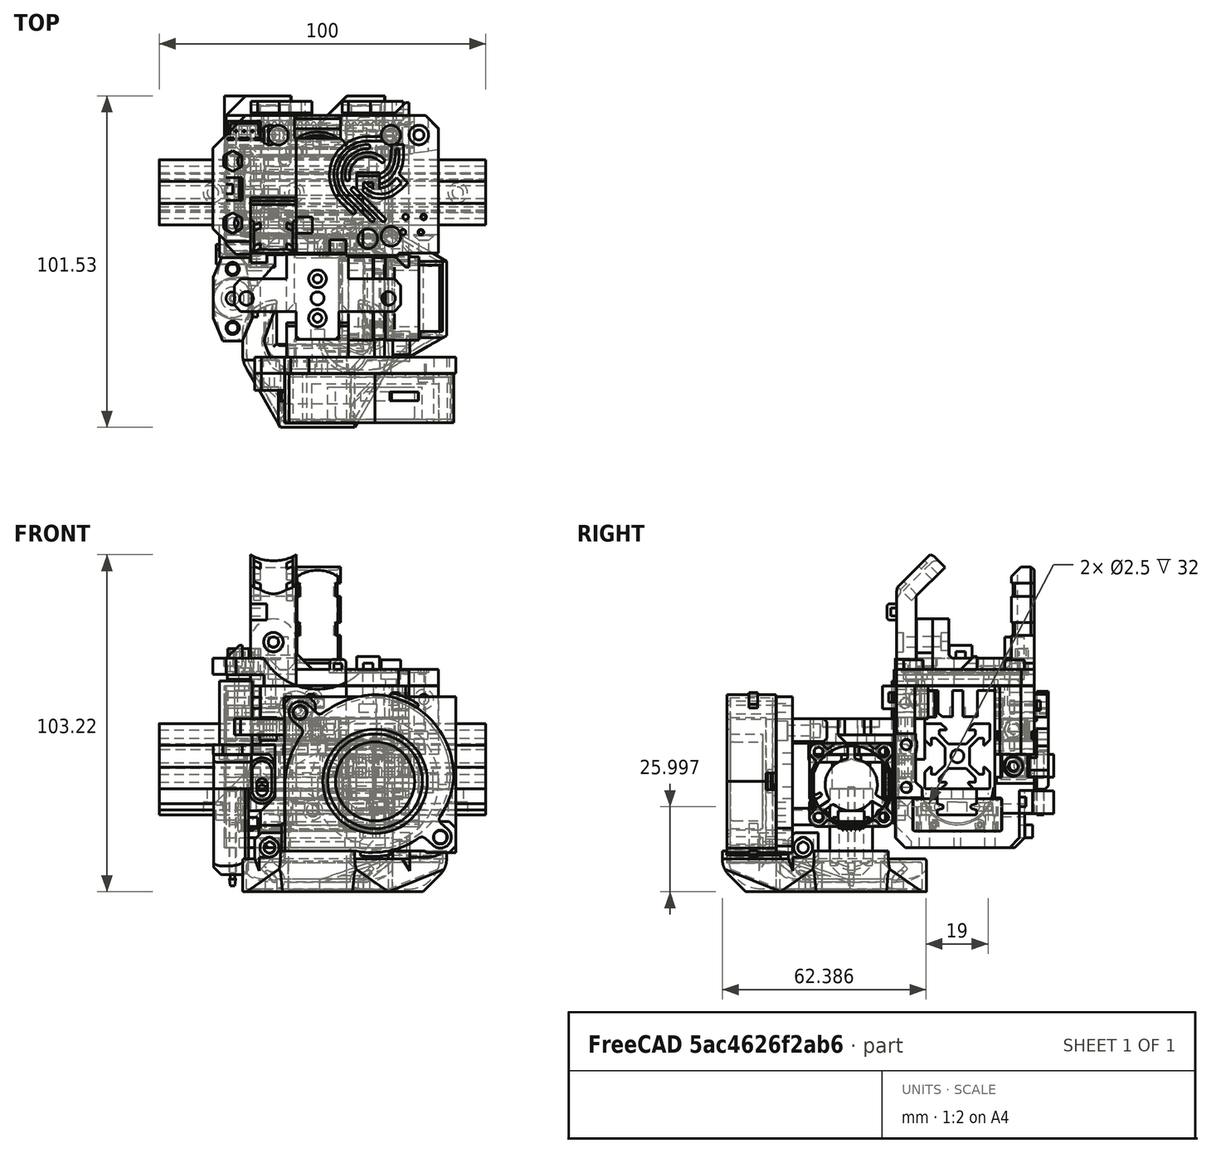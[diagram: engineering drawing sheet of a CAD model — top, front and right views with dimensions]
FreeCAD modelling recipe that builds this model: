
FCSTD DOCUMENT  (FreeCAD 0.18R16146 (Git))
Label: mosquito-mount
License: All rights reserved
LicenseURL: http://en.wikipedia.org/wiki/All_rights_reserved
objects: Part::Box×89, Part::Cylinder×71, Part::Cut×71, Part::MultiFuse×55, Part::Chamfer×54, Part::Feature×39, Mesh::Feature×1
note: 379 computed .brp shape members not serialized (recipe doc carries the construction recipe); baked Part::Feature solids carry a one-line shape summary decoded from their .brp

FEATURE [Part::Box] Box  label="Cube"
  AttacherType = Attacher::AttachEngine3D
  Height = 10
  Length = 45.4
  Width = 27
FEATURE [Part::Cylinder] Cylinder
  Angle = 360
  AttacherType = Attacher::AttachEngine3D
  Height = 10
  Placement = pos=(12.7,3.5,0) rot=(0,0,1;0rad)
  Radius = 2
FEATURE [Part::Cylinder] Cylinder001
  Angle = 360
  AttacherType = Attacher::AttachEngine3D
  Height = 10
  Placement = pos=(32.7,3.5,0) rot=(0,0,1;0rad)
  Radius = 2
FEATURE [Part::Cylinder] Cylinder002
  Angle = 360
  AttacherType = Attacher::AttachEngine3D
  Height = 10
  Placement = pos=(32.7,23.5,0) rot=(0,0,1;0rad)
  Radius = 2
FEATURE [Part::Cylinder] Cylinder003
  Angle = 360
  AttacherType = Attacher::AttachEngine3D
  Height = 10
  Placement = pos=(12.7,23.5,0) rot=(0,0,1;0rad)
  Radius = 2
FEATURE [Part::MultiFuse] Fusion
  Shapes = -> [Cylinder003,Cylinder002,Cylinder001,Cylinder]
FEATURE [Part::Cut] Cut  label="12H-block-ref"
  Base = -> Box
  Placement = pos=(-22.7,-13.5,5) rot=(0,0,1;0rad)
  Tool = -> Fusion
FEATURE [Part::Feature] Part__Feature072001  label="hemera-mount"
  shape: bbox 65.55 x 51.14 x 89.74 mm, 349 faces (baked)
FEATURE [Part::Feature] Part__Feature  label="mosquito"
  Placement = pos=(-7e-15,-32.5,3.5) rot=(1,0,0;1.5708rad)
  shape: bbox 18.85 x 27 x 47 mm, 429 faces, 0 solids (baked)
FEATURE [Part::Box] Box001  label="Cube001"
  AttacherType = Attacher::AttachEngine3D
  Height = 49.5
  Length = 56
  Placement = pos=(-28,-19,0) rot=(0,0,1;0rad)
  Width = 38
FEATURE [Part::Box] Box004  label="block-slot"
  AttacherType = Attacher::AttachEngine3D
  Height = 10.2
  Length = 60
  Placement = pos=(-22.8,-13.6,5) rot=(0,0,1;0rad)
  Width = 27.2
FEATURE [Part::Cylinder] Cylinder004
  Angle = 360
  AttacherType = Attacher::AttachEngine3D
  Height = 26
  Placement = pos=(-12,0,18) rot=(0,-1,0;1.5708rad)
  Radius = 11
FEATURE [Part::Box] Box005  label="Cube002"
  AttacherType = Attacher::AttachEngine3D
  Height = 39
  Length = 72
  Placement = pos=(-32,-13.05,18) rot=(0,0,1;0rad)
  Width = 24.5
FEATURE [Part::Chamfer] Chamfer
  Base = -> Box005
  Edges = 1 edges r=2: [Edge9]
  Placement = pos=(0,0,0.1) rot=(0,0,1;0rad)
FEATURE [Part::Chamfer] Chamfer001
  Base = -> Box004
  Edges = 4 edges r=0.4: [Edge9,Edge10,Edge11,Edge12]
FEATURE [Part::Box] Box006  label="Cube003"
  AttacherType = Attacher::AttachEngine3D
  Height = 10
  Length = 56
  Placement = pos=(-22.8,-11,10) rot=(0,0,1;0rad)
  Width = 22
FEATURE [Mesh::Feature] sherpa_mini_assy_a1
  Placement = pos=(-4.35,-22.5,53) rot=(1,0,0;1.5708rad)
FEATURE [Part::Cut] Cut001
  Base = -> Box001
  Tool = -> Chamfer001
FEATURE [Part::Cut] Cut002
  Base = -> Cut001
  Tool = -> Box006
FEATURE [Part::Cut] Cut003
  Base = -> Cut002
  Tool = -> Cylinder004
FEATURE [Part::Cut] Cut004
  Base = -> Cut003
  Tool = -> Chamfer
FEATURE [Part::Box] Box007  label="Cube004"
  AttacherType = Attacher::AttachEngine3D
  Height = 32.15
  Length = 56
  Placement = pos=(-28,19,17.35) rot=(0,0,1;0rad)
  Width = 4.53
FEATURE [Part::Box] Box008  label="Cube005"
  AttacherType = Attacher::AttachEngine3D
  Height = 6.97
  Length = 22
  Placement = pos=(-1.5,18.5,10.38) rot=(0,0,1;0rad)
  Width = 11
FEATURE [Part::Box] Box009  label="Cube006"
  AttacherType = Attacher::AttachEngine3D
  Height = 6.97
  Length = 20
  Placement = pos=(-28,23.5,21.6) rot=(0,0,1;0rad)
  Width = 6
FEATURE [Part::Box] Box010  label="Cube007"
  AttacherType = Attacher::AttachEngine3D
  Height = 6.97
  Length = 6
  Placement = pos=(10.5,23.5,10.38) rot=(0,0,1;0rad)
  Width = 3
FEATURE [Part::Box] Box011  label="Cube008"
  AttacherType = Attacher::AttachEngine3D
  Height = 6.97
  Length = 6
  Placement = pos=(-17.5,23.5,21.6) rot=(0,0,1;0rad)
  Width = 3
FEATURE [Part::Cut] Cut005
  Base = -> Box009
  Tool = -> Box011
FEATURE [Part::Cut] Cut006
  Base = -> Box008
  Tool = -> Box010
FEATURE [Part::Chamfer] Chamfer002
  Base = -> Cut006
  Edges = 1 edges r=10.5: [Edge3]
FEATURE [Part::Chamfer] Chamfer003
  Base = -> Cut005
  Edges = 1 edges r=5.97: [Edge3]
FEATURE [Part::Box] Box012  label="Cube009"
  AttacherType = Attacher::AttachEngine3D
  Height = 10
  Length = 12
  Placement = pos=(-24,-1,0) rot=(0,0,1;0rad)
  Width = 2
FEATURE [Part::Cut] Cut007
  Base = -> Cut004
  Tool = -> Box012
FEATURE [Part::MultiFuse] Fusion001
  Shapes = -> [Cut007,Box007]
FEATURE [Part::Box] Box013  label="Cube010"
  AttacherType = Attacher::AttachEngine3D
  Height = 6.97
  Length = 29
  Placement = pos=(-28,3.61,32.63) rot=(0,0,1;0rad)
  Width = 10
FEATURE [Part::Box] Box014  label="Cube011"
  AttacherType = Attacher::AttachEngine3D
  Height = 6.97
  Length = 23
  Placement = pos=(5,3.61,21.6) rot=(0,0,1;0rad)
  Width = 10
FEATURE [Part::Box] Box015  label="Cube012"
  AttacherType = Attacher::AttachEngine3D
  Height = 6.97
  Length = 17
  Placement = pos=(-8,9,21.6) rot=(0,0,1;0rad)
  Width = 22
FEATURE [Part::Box] Box016  label="Cube013"
  AttacherType = Attacher::AttachEngine3D
  Height = 6.97
  Length = 17
  Placement = pos=(1,7.5,32.63) rot=(0,0,1;0rad)
  Width = 20
FEATURE [Part::Cut] Cut008
  Base = -> Fusion001
  Tool = -> Box016
FEATURE [Part::Cut] Cut009
  Base = -> Cut008
  Tool = -> Box015
FEATURE [Part::Box] Box017  label="Cube014"
  AttacherType = Attacher::AttachEngine3D
  Height = 6.97
  Length = 23
  Placement = pos=(5,20.61,21.6) rot=(0,0,1;0rad)
  Width = 10
FEATURE [Part::Box] Box018  label="Cube015"
  AttacherType = Attacher::AttachEngine3D
  Height = 5.97
  Length = 29
  Placement = pos=(-28,20.61,33.63) rot=(0,0,1;0rad)
  Width = 10
FEATURE [Part::Cut] Cut010
  Base = -> Cut009
  Tool = -> Box013
FEATURE [Part::Cut] Cut011
  Base = -> Cut010
  Tool = -> Box014
FEATURE [Part::Feature] Part__Feature072001001  label="hemera-mount001"
  shape: bbox 65.55 x 51.14 x 89.74 mm, 349 faces (baked)
FEATURE [Part::Feature] Part__Feature072001002  label="hemera-mount002"
  shape: bbox 65.55 x 51.14 x 89.74 mm, 349 faces (baked)
FEATURE [Part::Cut] Cut012
  Base = -> Box017
  Tool = -> Part__Feature072001002
FEATURE [Part::Cut] Cut013
  Base = -> Box018
  Tool = -> Part__Feature072001001
FEATURE [Part::Feature] Cut013001  label="Cut014"
  Placement = pos=(0,0,-1) rot=(0,0,1;0rad)
  shape: bbox 29 x 10 x 5.971 mm, 63 faces (baked)
FEATURE [Part::Cut] Cut013002
  Base = -> Cut011
  Tool = -> Cut012
FEATURE [Part::MultiFuse] Fusion002
  Shapes = -> [Cut013001,Cut013]
FEATURE [Part::Cut] Cut013003
  Base = -> Cut013002
  Tool = -> Fusion002
FEATURE [Part::Cylinder] Cylinder005
  Angle = 360
  AttacherType = Attacher::AttachEngine3D
  Height = 6
  Placement = pos=(-5,17.57,36.115) rot=(0,1,0;1.5708rad)
  Radius = 2.1
FEATURE [Part::Cylinder] Cylinder006
  Angle = 360
  AttacherType = Attacher::AttachEngine3D
  Height = 6
  Placement = pos=(9,17.57,25.08) rot=(0,1,0;1.5708rad)
  Radius = 2.1
FEATURE [Part::Cylinder] Cylinder007
  Angle = 360
  AttacherType = Attacher::AttachEngine3D
  Height = 32
  Placement = pos=(-6e-15,17.57,25.08) rot=(0,1,0;1.5708rad)
  Radius = 1.65
FEATURE [Part::Cylinder] Cylinder008
  Angle = 360
  AttacherType = Attacher::AttachEngine3D
  Height = 37
  Placement = pos=(-29,17.57,36.115) rot=(0,1,0;1.5708rad)
  Radius = 1.65
FEATURE [Part::Cut] Cut013004
  Base = -> Cut013003
  Tool = -> Cylinder008
FEATURE [Part::Cut] Cut013005
  Base = -> Cut013004
  Tool = -> Cylinder007
FEATURE [Part::Cylinder] Cylinder009
  Angle = 360
  AttacherType = Attacher::AttachEngine3D
  Height = 3
  Placement = pos=(25,17.57,25.08) rot=(0,1,0;1.5708rad)
  Radius = 3
FEATURE [Part::Cylinder] Cylinder010
  Angle = 360
  AttacherType = Attacher::AttachEngine3D
  Height = 3
  Placement = pos=(-28,17.57,36.115) rot=(0,1,0;1.5708rad)
  Radius = 3
FEATURE [Part::MultiFuse] Fusion003
  Shapes = -> [Cylinder010,Cylinder009]
FEATURE [Part::Cut] Cut013006
  Base = -> Cut013005
  Tool = -> Fusion003
FEATURE [Part::MultiFuse] Fusion004
  Shapes = -> [Cylinder006,Cylinder005]
FEATURE [Part::Cut] Cut013007
  Base = -> Cut013006
  Tool = -> Fusion004
FEATURE [Part::Box] Box019  label="Cube016"
  AttacherType = Attacher::AttachEngine3D
  Height = 19.65
  Length = 10.5
  Placement = pos=(17.5,-20.5,15.2) rot=(0,0,1;0rad)
  Width = 10
FEATURE [Part::Box] Box020  label="Cube017"
  AttacherType = Attacher::AttachEngine3D
  Height = 28
  Length = 10.5
  Placement = pos=(-28,-20,26) rot=(0,0,1;0rad)
  Width = 10
FEATURE [Part::Cylinder] Cylinder011
  Angle = 360
  AttacherType = Attacher::AttachEngine3D
  Height = 14.5
  Placement = pos=(3,-15.83,18.41) rot=(0,1,0;1.5708rad)
  Radius = 1.65
FEATURE [Part::Cylinder] Cylinder012
  Angle = 360
  AttacherType = Attacher::AttachEngine3D
  Height = 14.5
  Placement = pos=(3,-15.83,31.54) rot=(0,1,0;1.5708rad)
  Radius = 1.65
FEATURE [Part::Feature] Part__Feature044  label="duct-pos-pref"
  Placement = pos=(0.025,-32.5,-13.5) rot=(0,0,1;1.5708rad)
  shape: bbox 38.99 x 46.01 x 18.01 mm, 128 faces (baked)
FEATURE [Part::Cylinder] Cylinder013
  Angle = 360
  AttacherType = Attacher::AttachEngine3D
  Height = 14.5
  Placement = pos=(-3,-15.82,29.97) rot=(0,-1,0;1.5708rad)
  Radius = 1.65
FEATURE [Part::Cylinder] Cylinder014
  Angle = 360
  AttacherType = Attacher::AttachEngine3D
  Height = 19.5
  Placement = pos=(2,-15.82,44.28) rot=(0,-1,0;1.5708rad)
  Radius = 1.65
FEATURE [Part::Cylinder] Cylinder015
  Angle = 360
  AttacherType = Attacher::AttachEngine3D
  Height = 19.5
  Placement = pos=(2,-15.82,44.28) rot=(0,-1,0;1.5708rad)
  Radius = 3
FEATURE [Part::Cylinder] Cylinder016
  Angle = 360
  AttacherType = Attacher::AttachEngine3D
  Height = 14.5
  Placement = pos=(-3,-15.82,29.97) rot=(0,-1,0;1.5708rad)
  Radius = 3
FEATURE [Part::Cylinder] Cylinder017
  Angle = 360
  AttacherType = Attacher::AttachEngine3D
  Height = 14.5
  Placement = pos=(3,-15.83,31.54) rot=(0,1,0;1.5708rad)
  Radius = 3
FEATURE [Part::Cylinder] Cylinder018
  Angle = 360
  AttacherType = Attacher::AttachEngine3D
  Height = 14.5
  Placement = pos=(3,-15.83,18.41) rot=(0,1,0;1.5708rad)
  Radius = 3
FEATURE [Part::Box] Box021  label="Cube018"
  AttacherType = Attacher::AttachEngine3D
  Height = 5.5
  Length = 2
  Placement = pos=(10,-23.5,28.79) rot=(0,0,1;0rad)
  Width = 20
FEATURE [Part::Box] Box022  label="Cube019"
  AttacherType = Attacher::AttachEngine3D
  Height = 5.5
  Length = 2
  Placement = pos=(-3,-23.5,41.53) rot=(0,0,1;0rad)
  Width = 20
FEATURE [Part::Box] Box023  label="Cube020"
  AttacherType = Attacher::AttachEngine3D
  Height = 5.5
  Length = 2
  Placement = pos=(-10,-23.5,27.22) rot=(0,0,1;0rad)
  Width = 20
FEATURE [Part::Box] Box024  label="Cube021"
  AttacherType = Attacher::AttachEngine3D
  Height = 5.5
  Length = 2
  Placement = pos=(8,-23.5,15.66) rot=(0,0,1;0rad)
  Width = 20
FEATURE [Part::Box] Box025  label="Cube022"
  AttacherType = Attacher::AttachEngine3D
  Height = 10
  Length = 10
  Placement = pos=(18,-13.5,39.5) rot=(0,0,1;0rad)
  Width = 4.5
FEATURE [Part::Chamfer] Chamfer004  label="top-atd"
  Base = -> Box025
  Edges = 1 edges r=4.05: [Edge3]
FEATURE [Part::Feature] Fusion015  label="bltouch-pref"
  Placement = pos=(-26,-32.5,28.45) rot=(0,0,-1;4.71239rad)
  shape: bbox 16.68 x 26.66 x 40.15 mm, 80 faces (baked)
FEATURE [Part::Cylinder] Cylinder019
  Angle = 360
  AttacherType = Attacher::AttachEngine3D
  Height = 26
  Placement = pos=(-6.45,1e-14,43.07) rot=(-1,0,0;1.5708rad)
  Radius = 1.65
FEATURE [Part::Cylinder] Cylinder020
  Angle = 360
  AttacherType = Attacher::AttachEngine3D
  Height = 26
  Placement = pos=(21.55,1.2e-14,31.84) rot=(-1,0,0;1.5708rad)
  Radius = 1.65
FEATURE [Part::Cylinder] Cylinder021
  Angle = 360
  AttacherType = Attacher::AttachEngine3D
  Height = 6
  Placement = pos=(-6.45,11.45,43.07) rot=(-1,0,0;1.5708rad)
  Radius = 2.1
FEATURE [Part::Cylinder] Cylinder022
  Angle = 360
  AttacherType = Attacher::AttachEngine3D
  Height = 6
  Placement = pos=(21.55,11.45,31.84) rot=(-1,0,0;1.5708rad)
  Radius = 2.1
FEATURE [Part::MultiFuse] Fusion018
  Shapes = -> [Cylinder020,Cylinder019]
FEATURE [Part::MultiFuse] Fusion019
  Shapes = -> [Cylinder022,Cylinder021]
FEATURE [Part::Cut] Cut013013
  Base = -> Cut013007
  Tool = -> Box020
FEATURE [Part::MultiFuse] Fusion026  label="back-bolt"
  Shapes = -> [Fusion019,Fusion018]
FEATURE [Part::Box] Box033  label="Cube030"
  AttacherType = Attacher::AttachEngine3D
  Height = 5
  Length = 51
  Placement = pos=(-25.5,-36.5,34.5) rot=(0,0,1;0rad)
  Width = 10
FEATURE [Part::Box] Box037  label="Cube034"
  AttacherType = Attacher::AttachEngine3D
  Height = 3
  Length = 12
  Placement = pos=(-32,-45.5,28.5) rot=(0,0,1;0rad)
  Width = 26.5
FEATURE [Part::Box] Box038  label="Cube035"
  AttacherType = Attacher::AttachEngine3D
  Height = 18
  Length = 9.5
  Placement = pos=(-22.5,-22,13.5) rot=(0,0,1;0rad)
  Width = 3
FEATURE [Part::Box] Box039  label="Cube036"
  AttacherType = Attacher::AttachEngine3D
  Height = 3
  Length = 8
  Placement = pos=(-21,-30,28.5) rot=(0,0,1;0rad)
  Width = 9
FEATURE [Part::Box] Box041  label="Cube038"
  AttacherType = Attacher::AttachEngine3D
  Height = 6
  Length = 3
  Placement = pos=(-18.65,-22,15.5) rot=(0,0,-1;1.5708rad)
  Width = 3.3
FEATURE [Part::Cylinder] Cylinder023
  Angle = 360
  AttacherType = Attacher::AttachEngine3D
  Height = 3
  Placement = pos=(-17,-22,21.5) rot=(0.57735,-0.57735,0.57735;2.0944rad)
  Radius = 1.65
FEATURE [Part::Cylinder] Cylinder024
  Angle = 360
  AttacherType = Attacher::AttachEngine3D
  Height = 3
  Placement = pos=(-17,-22,15.5) rot=(0.57735,-0.57735,0.57735;2.0944rad)
  Radius = 1.65
FEATURE [Part::Box] Box042  label="Cube039"
  AttacherType = Attacher::AttachEngine3D
  Height = 15
  Length = 2.25
  Placement = pos=(-20.1,-20,12) rot=(0,0,1;0rad)
  Width = 2.1
FEATURE [Part::Box] Box043  label="Cube040"
  AttacherType = Attacher::AttachEngine3D
  Height = 7
  Length = 2
  Placement = pos=(-20,-20,18.5) rot=(0,0,1;0rad)
  Width = 2
FEATURE [Part::Chamfer] Chamfer005009
  Base = -> Box043
  Edges = 1 edges r=1: [Edge7]
FEATURE [Part::Box] Box044  label="Cube041"
  AttacherType = Attacher::AttachEngine3D
  Height = 2
  Length = 2
  Placement = pos=(-20,-19,25.5) rot=(0,0,1;0rad)
  Width = 2
FEATURE [Part::Chamfer] Chamfer005010
  Base = -> Box044
  Edges = 1 edges r=1: [Edge9]
  Placement = pos=(0,0,-1) rot=(0,0,1;0rad)
FEATURE [Part::Cut] Cut013021
  Base = -> Chamfer005009
  Placement = pos=(-2.5,0,-3) rot=(0,0,1;0rad)
  Tool = -> Chamfer005010
FEATURE [Part::Chamfer] Chamfer005011
  Base = -> Box042
  Edges = 1 edges r=1.15: [Edge7]
  Placement = pos=(-2.5,0,0) rot=(0,0,1;0rad)
FEATURE [Part::MultiFuse] Fusion030
  Placement = pos=(0,3,2) rot=(0,0,1;0rad)
  Shapes = -> [Box041,Cylinder024,Cylinder023]
FEATURE [Part::Cylinder] Cylinder025
  Angle = 360
  AttacherType = Attacher::AttachEngine3D
  Height = 5
  Placement = pos=(-17,-14,20.5) rot=(1,0,0;1.5708rad)
  Radius = 2.1
FEATURE [Part::Chamfer] Chamfer005016
  Base = -> Box037
  Edges = 1 edges: [Edge1 r1=7 r2=3]
FEATURE [Part::Chamfer] Chamfer005017
  Base = -> Chamfer005016
  Edges = 1 edges: [Edge15 r1=3 r2=7]
FEATURE [Part::Chamfer] Chamfer005018
  Base = -> Chamfer005017
  Edges = 1 edges: [Edge16 r1=7 r2=3]
FEATURE [Part::Cylinder] Cylinder026
  Angle = 360
  AttacherType = Attacher::AttachEngine3D
  Height = 10
  Placement = pos=(-26,-32.5,25) rot=(0,0,1;0rad)
  Radius = 2
FEATURE [Part::Cylinder] Cylinder027
  Angle = 360
  AttacherType = Attacher::AttachEngine3D
  Height = 10
  Placement = pos=(-26,-23.5,25) rot=(0,0,1;0rad)
  Radius = 2.05
FEATURE [Part::Cylinder] Cylinder028
  Angle = 360
  AttacherType = Attacher::AttachEngine3D
  Height = 10
  Placement = pos=(-26,-41.5,25) rot=(0,0,1;0rad)
  Radius = 2.05
FEATURE [Part::MultiFuse] Fusion033
  Shapes = -> [Cylinder028,Cylinder027,Cylinder026]
FEATURE [Part::Cut] Cut013027
  Base = -> Chamfer005018
  Tool = -> Fusion033
FEATURE [Part::Chamfer] Chamfer005019
  Base = -> Box038
  Edges = 1 edges r=1: [Edge1]
FEATURE [Part::Chamfer] Chamfer005020
  Base = -> Chamfer005019
  Edges = 1 edges r=2: [Edge14]
FEATURE [Part::Cut] Cut013028
  Base = -> Chamfer005020
  Tool = -> Fusion030
FEATURE [Part::Chamfer] Chamfer005021
  Base = -> Box039
  Edges = 1 edges: [Edge5 r1=8 r2=7]
FEATURE [Part::Box] Box045  label="Cube042"
  AttacherType = Attacher::AttachEngine3D
  Height = 3
  Length = 8.5
  Placement = pos=(-21.5,-24,26.5) rot=(0,0,1;0rad)
  Width = 3
FEATURE [Part::Box] Box046  label="Cube043"
  AttacherType = Attacher::AttachEngine3D
  Height = 3
  Length = 8.5
  Placement = pos=(-4.5,-28,28.5) rot=(0,0,1;0rad)
  Width = 6
FEATURE [Part::Feature] Chamfer005021001  label="Chamfer005022"
  Placement = pos=(12,0,0) rot=(0,0,1;0rad)
  shape: bbox 8 x 9 x 3 mm, 7 faces (baked)
FEATURE [Part::Cut] Cut013029
  Base = -> Box046
  Placement = pos=(-12,0,-2) rot=(0,0,1;0rad)
  Tool = -> Chamfer005021001
FEATURE [Part::Chamfer] Chamfer005021002
  Base = -> Box045
  Edges = 1 edges r=2: [Edge9]
FEATURE [Part::Cut] Cut013030
  Base = -> Chamfer005021002
  Tool = -> Cut013029
FEATURE [Part::MultiFuse] Fusion034  label="probe-mount-base"
  Shapes = -> [Cut013030,Cut013021,Chamfer005021,Cut013027,Cut013028]
FEATURE [Part::Cylinder] Cylinder030
  Angle = 360
  AttacherType = Attacher::AttachEngine3D
  Height = 10
  Placement = pos=(-10,10,0) rot=(0,0,1;0rad)
  Radius = 1.6
FEATURE [Part::Cylinder] Cylinder031
  Angle = 360
  AttacherType = Attacher::AttachEngine3D
  Height = 10
  Placement = pos=(10,-10,0) rot=(0,0,1;0rad)
  Radius = 1.6
FEATURE [Part::Cylinder] Cylinder032
  Angle = 360
  AttacherType = Attacher::AttachEngine3D
  Height = 10
  Placement = pos=(10,10,0) rot=(0,0,1;0rad)
  Radius = 1.6
FEATURE [Part::Cylinder] Cylinder033
  Angle = 360
  AttacherType = Attacher::AttachEngine3D
  Height = 10
  Placement = pos=(-10,-10,0) rot=(0,0,1;0rad)
  Radius = 1.6
FEATURE [Part::Feature] Fusion036001  label="rail-bolt001"
  shape: bbox 23.2 x 23.2 x 10 mm, 12 faces, 4 solids (baked)
FEATURE [Part::Box] Box048  label="Cube045"
  AttacherType = Attacher::AttachEngine3D
  Height = 7.5
  Length = 13
  Placement = pos=(-6.5,-45,32) rot=(0,0,1;0rad)
  Width = 18.5
FEATURE [Part::Chamfer] Chamfer005021006  label="Chamfer005021007"
  Base = -> Box033
  Edges = 4 edges r=2: [Edge1,Edge3,Edge5,Edge7]
FEATURE [Part::Cylinder] Cylinder036
  Angle = 360
  AttacherType = Attacher::AttachEngine3D
  Height = 10
  Placement = pos=(-21.75,-32.5,34.5) rot=(0,0,1;0rad)
  Radius = 2.1
FEATURE [Part::Cylinder] Cylinder037
  Angle = 360
  AttacherType = Attacher::AttachEngine3D
  Height = 13
  Placement = pos=(0,-32.5,31.5) rot=(0,0,1;0rad)
  Radius = 2
FEATURE [Part::Cylinder] Cylinder038
  Angle = 360
  AttacherType = Attacher::AttachEngine3D
  Height = 10
  Placement = pos=(21.75,-32.5,34.5) rot=(0,0,1;0rad)
  Radius = 2.1
FEATURE [Part::Cylinder] Cylinder039
  Angle = 360
  AttacherType = Attacher::AttachEngine3D
  Height = 13
  Placement = pos=(0,-38.5,31.5) rot=(0,0,1;0rad)
  Radius = 1.3
FEATURE [Part::Cylinder] Cylinder042
  Angle = 360
  AttacherType = Attacher::AttachEngine3D
  Height = 13
  Placement = pos=(0,-26.5,31.5) rot=(0,0,1;0rad)
  Radius = 1.3
FEATURE [Part::MultiFuse] Fusion036004
  Shapes = -> [Cylinder036,Cylinder038]
FEATURE [Part::Cut] Cut013037
  Base = -> Chamfer005021006
  Tool = -> Fusion036004
FEATURE [Part::Cylinder] Cylinder045
  Angle = 360
  AttacherType = Attacher::AttachEngine3D
  Height = 3
  Placement = pos=(0,-26.5,37) rot=(0,0,1;0rad)
  Radius = 2.7
FEATURE [Part::Cylinder] Cylinder046
  Angle = 360
  AttacherType = Attacher::AttachEngine3D
  Height = 3
  Placement = pos=(0,-38.5,37) rot=(0,0,1;0rad)
  Radius = 2.7
FEATURE [Part::Cylinder] Cylinder047
  Angle = 360
  AttacherType = Attacher::AttachEngine3D
  Height = 13
  Placement = pos=(-22.45,-9.5,36) rot=(0,0,1;0rad)
  Radius = 2.05
FEATURE [Part::Cylinder] Cylinder048
  Angle = 360
  AttacherType = Attacher::AttachEngine3D
  Height = 13
  Placement = pos=(-22.45,9.5,48) rot=(0,0,1;0rad)
  Radius = 2.05
FEATURE [Part::Box] Box053  label="Cube050"
  AttacherType = Attacher::AttachEngine3D
  Height = 5
  Length = 44.5
  Placement = pos=(-16.5,-19,49.5) rot=(0,0,1;0rad)
  Width = 42.53
FEATURE [Part::Box] Box054  label="Cube051"
  AttacherType = Attacher::AttachEngine3D
  Height = 10
  Length = 12
  Placement = pos=(-31,4.5,43.5) rot=(0,0,1;0rad)
  Width = 10
FEATURE [Part::Box] Box055  label="Cube052"
  AttacherType = Attacher::AttachEngine3D
  Height = 5
  Length = 16.5
  Placement = pos=(-28,-19,53) rot=(0,0,1;0rad)
  Width = 42.53
FEATURE [Part::Chamfer] Chamfer005021009  label="Chamfer005021010"
  Base = -> Box054
  Edges = 1 edges r=3: [Edge7]
  Placement = pos=(1,0,0) rot=(0,0,1;0rad)
FEATURE [Part::Feature] Fusion036012001  label="sensor001"
  Placement = pos=(-22.5,3.95,51.5) rot=(0,0,-1;1.5708rad)
  shape: bbox 10.3 x 33 x 12.93 mm, 36 faces (baked)
FEATURE [Part::Chamfer] Chamfer005021010  label="Chamfer005021011"
  Base = -> Box055
  Edges = 1 edges r=3.5: [Edge6]
FEATURE [Part::Chamfer] Chamfer005021011  label="Chamfer005021012"
  Base = -> Chamfer005021010
  Edges = 1 edges r=3: [Edge8]
FEATURE [Part::Cylinder] Cylinder049  label="motor-cut"
  Angle = 360
  AttacherType = Attacher::AttachEngine3D
  Height = 19
  Placement = pos=(0,-20,67.5) rot=(-1,0,0;1.5708rad)
  Radius = 19
FEATURE [Part::Cylinder] Cylinder050
  Angle = 360
  AttacherType = Attacher::AttachEngine3D
  Height = 19
  Placement = pos=(0,-20,67.5) rot=(-1,0,0;1.5708rad)
  Radius = 19
FEATURE [Part::Cylinder] Cylinder051
  Angle = 360
  AttacherType = Attacher::AttachEngine3D
  Height = 6
  Placement = pos=(22.5,-13.5,51.5) rot=(0,0,1;0rad)
  Radius = 3
FEATURE [Part::Cylinder] Cylinder052
  Angle = 360
  AttacherType = Attacher::AttachEngine3D
  Height = 6
  Placement = pos=(22.5,17.5,51.5) rot=(0,0,1;0rad)
  Radius = 3
FEATURE [Part::Cylinder] Cylinder053
  Angle = 360
  AttacherType = Attacher::AttachEngine3D
  Height = 10
  Placement = pos=(-12,17.5,51.5) rot=(0,0,1;0rad)
  Radius = 3
FEATURE [Part::Cylinder] Cylinder054
  Angle = 360
  AttacherType = Attacher::AttachEngine3D
  Height = 6
  Placement = pos=(-12,17.5,43.5) rot=(0,0,1;0rad)
  Radius = 2.1
FEATURE [Part::Cylinder] Cylinder055
  Angle = 360
  AttacherType = Attacher::AttachEngine3D
  Height = 6
  Placement = pos=(22.5,17.5,43.5) rot=(0,0,1;0rad)
  Radius = 2.1
FEATURE [Part::Cylinder] Cylinder056
  Angle = 360
  AttacherType = Attacher::AttachEngine3D
  Height = 6
  Placement = pos=(22.5,-13.5,43.5) rot=(0,0,1;0rad)
  Radius = 2.1
FEATURE [Part::Cylinder] Cylinder057
  Angle = 360
  AttacherType = Attacher::AttachEngine3D
  Height = 6
  Placement = pos=(22.5,-13.5,48.5) rot=(0,0,1;0rad)
  Radius = 1.65
FEATURE [Part::Cylinder] Cylinder058
  Angle = 360
  AttacherType = Attacher::AttachEngine3D
  Height = 10
  Placement = pos=(-12,17.5,49.5) rot=(0,0,1;0rad)
  Radius = 1.65
FEATURE [Part::Cylinder] Cylinder059
  Angle = 360
  AttacherType = Attacher::AttachEngine3D
  Height = 6
  Placement = pos=(22.5,17.5,48.5) rot=(0,0,1;0rad)
  Radius = 1.65
FEATURE [Part::MultiFuse] Fusion036012010  label="top-bolt-slot"
  Shapes = -> [Cylinder056,Cylinder055,Cylinder054]
FEATURE [Part::MultiFuse] Fusion036012011
  Shapes = -> [Cylinder059,Cylinder058,Cylinder057]
FEATURE [Part::Feature] Part__Feature090001002  label="X_BeltHolder_LH002"
  Placement = pos=(11.44,0.35,12.0001) rot=(0,0,1;0rad)
  shape: bbox 7.277 x 6.5 x 22.78 mm, 35 faces (baked)
FEATURE [Part::Feature] Part__Feature112001001  label="X_BeltHolderFL_Hemera002"
  Placement = pos=(0,0,-0.3) rot=(0,0,1;0rad)
  shape: bbox 8.346 x 8.354 x 19.65 mm, 38 faces (baked)
FEATURE [Part::Feature] Cut036009013017007008001  label="belt-holder-r002"
  Placement = pos=(22.2,27.9,86.4) rot=(1,0,0;1.5708rad)
  shape: bbox 18.69 x 5.87 x 26.47 mm, 29 faces (baked)
FEATURE [Part::Feature] Cut036009013017007008002  label="belt-holder-r003"
  Placement = pos=(-5.7,27.9,97.8) rot=(1,0,0;1.5708rad)
  shape: bbox 18.69 x 5.87 x 26.47 mm, 29 faces (baked)
FEATURE [Part::Box] Box056  label="Cube053"
  AttacherType = Attacher::AttachEngine3D
  Height = 7
  Length = 10
  Placement = pos=(17.5,-29,21.43) rot=(0,0,1;0rad)
  Width = 10
FEATURE [Part::Box] Box057  label="Cube054"
  AttacherType = Attacher::AttachEngine3D
  Height = 7
  Length = 10
  Placement = pos=(-27.5,-13.05,32.91) rot=(0,0,1;0rad)
  Width = 10
FEATURE [Part::Box] Box058  label="Cube055"
  AttacherType = Attacher::AttachEngine3D
  Height = 7
  Length = 10
  Placement = pos=(-27.5,-29,32.91) rot=(0,0,1;0rad)
  Width = 10
FEATURE [Part::Box] Box059  label="Cube056"
  AttacherType = Attacher::AttachEngine3D
  Height = 7
  Length = 10
  Placement = pos=(17.5,-13.05,21.43) rot=(0,0,1;0rad)
  Width = 10
FEATURE [Part::Box] Box060  label="Cube057"
  AttacherType = Attacher::AttachEngine3D
  Height = 7
  Length = 10
  Placement = pos=(12.5,-28.5,21.43) rot=(0,0,1;0rad)
  Width = 10
FEATURE [Part::Box] Box061  label="Cube058"
  AttacherType = Attacher::AttachEngine3D
  Height = 7
  Length = 10
  Placement = pos=(-22.5,-28.5,32.91) rot=(0,0,1;0rad)
  Width = 10
FEATURE [Part::Chamfer] Chamfer005021012  label="Chamfer005021013"
  Base = -> Box056
  Edges = 1 edges r=1: [Edge3]
  Placement = pos=(-1,1,0) rot=(0,0,1;0rad)
FEATURE [Part::Chamfer] Chamfer005021013  label="Chamfer005021014"
  Base = -> Box059
  Edges = 1 edges r=1: [Edge1]
  Placement = pos=(-0.5,-1,0) rot=(0,0,1;0rad)
FEATURE [Part::Chamfer] Chamfer005021014  label="Chamfer005021015"
  Base = -> Box058
  Edges = 1 edges r=1: [Edge7]
  Placement = pos=(1,1,0) rot=(0,0,1;0rad)
FEATURE [Part::Chamfer] Chamfer005021015  label="Chamfer005021016"
  Base = -> Box057
  Edges = 1 edges r=1: [Edge5]
  Placement = pos=(0.5,-1,0) rot=(0,0,1;0rad)
FEATURE [Part::Feature] Fusion036012014
  Placement = pos=(-22.5,4,51.5) rot=(0,0,-1;1.5708rad)
  shape: bbox 10.3 x 34.26 x 9.89 mm, 110 faces (baked)
FEATURE [Part::Box] Box062  label="Cube059"
  AttacherType = Attacher::AttachEngine3D
  Height = 10
  Length = 14
  Placement = pos=(-30.5,14,52) rot=(0,0,1;0rad)
  Width = 11
FEATURE [Part::MultiFuse] Fusion036012015  label="end-stop-pref"
  Shapes = -> [Fusion036012014,Fusion036012001]
FEATURE [Part::Box] Box063002  label="Cube060"
  AttacherType = Attacher::AttachEngine3D
  Height = 7
  Length = 9
  Placement = pos=(23,30,0) rot=(0,0,1;0rad)
  Width = 7
FEATURE [Part::Box] Box063003  label="Cube061"
  AttacherType = Attacher::AttachEngine3D
  Height = 3
  Length = 5
  Placement = pos=(23,17,2) rot=(0,0,1;0rad)
  Width = 4
FEATURE [Part::Box] Box063004  label="Cube062"
  AttacherType = Attacher::AttachEngine3D
  Height = 7
  Length = 5
  Placement = pos=(23,19,0) rot=(0,0,1;0rad)
  Width = 4
FEATURE [Part::Cut] Cut036009013017007008007
  Base = -> Box063004
  Tool = -> Box063003
FEATURE [Part::Chamfer] Chamfer005021016  label="Chamfer005021017"
  Base = -> Box063002
  Edges = 1 edges r=4: [Edge5]
  Placement = pos=(-5,-11,0) rot=(0,0,1;0rad)
FEATURE [Part::Cut] Cut036009013017007008008  label="cable-mounter"
  Base = -> Cut036009013017007008007
  Placement = pos=(0,0,10.5) rot=(0,0,1;0rad)
  Tool = -> Chamfer005021016
FEATURE [Part::Feature] Cut036009013017007008008001  label="cable-mounter001"
  Placement = pos=(0,4.5,40) rot=(0,0,1;0rad)
  shape: bbox 5 x 4 x 7 mm, 10 faces (baked)
FEATURE [Part::Feature] Cut036009013017007008008002  label="cable-mounter002"
  Placement = pos=(0,0,10.5) rot=(0,0,1;0rad)
  shape: bbox 5 x 4 x 7 mm, 10 faces (baked)
FEATURE [Part::Feature] Cut001001  label="tesioner"
  Placement = pos=(0,14,33) rot=(0,0,1;0rad)
  shape: bbox 6.2 x 7.2 x 6.25 mm, 10 faces (baked)
FEATURE [Part::Feature] Cut036009013017007008008003  label="tesioner001"
  Placement = pos=(8,22.5,22) rot=(0,0,1;3.14159rad)
  shape: bbox 6.2 x 7.2 x 6.25 mm, 10 faces (baked)
FEATURE [Part::Feature] Cut036009013017007008008004  label="cable-mounter003"
  Placement = pos=(-51,15,39) rot=(1,0,0;1.5708rad)
  shape: bbox 5 x 7 x 4 mm, 10 faces (baked)
FEATURE [Part::Feature] Cut036009013017007008008005  label="cable-mounter004"
  Placement = pos=(1.5,-22,35.5) rot=(0.57735,0.57735,0.57735;2.0944rad)
  shape: bbox 7 x 5 x 4 mm, 10 faces (baked)
FEATURE [Part::Feature] Fusion036012021  label="2510-fan"
  Placement = pos=(6.52,-32.5,19.25) rot=(0.57735,0.57735,0.57735;2.0944rad)
  shape: bbox 10.5 x 25.76 x 25.8 mm, 132 faces, 2 solids (baked)
FEATURE [Part::Box] Box063005  label="Cube063"
  AttacherType = Attacher::AttachEngine3D
  Height = 2
  Length = 10
  Placement = pos=(-14.5,18,10.5) rot=(0,0,1;0rad)
  Width = 5
FEATURE [Part::Box] Box063006  label="Cube064"
  AttacherType = Attacher::AttachEngine3D
  Height = 2
  Length = 3
  Placement = pos=(-9.5,19,10.5) rot=(0,0,1;0rad)
  Width = 2
FEATURE [Part::Chamfer] Chamfer005021017  label="Chamfer005021018"
  Base = -> Box063005
  Edges = 1 edges r=4: [Edge3]
FEATURE [Part::Cut] Cut036009013017007008008006  label="extra-wire-mounter"
  Base = -> Chamfer005021017
  Placement = pos=(2.5,0,-2) rot=(0,0,1;0rad)
  Tool = -> Box063006
FEATURE [Part::Box] Box063014  label="Cube072"
  AttacherType = Attacher::AttachEngine3D
  Height = 27.5
  Length = 36
  Placement = pos=(-18,-24,-20.64) rot=(0,0,1;0rad)
  Width = 10
FEATURE [Part::Feature] Part__Feature090001001  label="X_CarriageTop_Hemera_Body002"
  Placement = pos=(0.2,-1.1,-3.3) rot=(0,0,1;0rad)
  shape: bbox 57.57 x 42.93 x 20.43 mm, 95 faces (baked)
FEATURE [Part::Feature] Part__Feature094001  label="X_CarriageEndStopMount_Body001"
  Placement = pos=(-0.7,-1.1,1) rot=(0,0,1;0rad)
  shape: bbox 25.48 x 38.63 x 17 mm, 44 faces (baked)
FEATURE [Part::MultiFuse] Fusion036012027
  Shapes = -> [Cylinder045,Cylinder042,Cylinder037,Cylinder046,Cylinder039]
FEATURE [Part::MultiFuse] Fusion036012028
  Shapes = -> [Box061,Box060]
FEATURE [Part::MultiFuse] Fusion036012013
  Shapes = -> [Chamfer005021012,Chamfer005021013,Chamfer005021014,Chamfer005021015]
FEATURE [Part::MultiFuse] Fusion036012029  label="front-belt-slot"
  Shapes = -> [Fusion036012013,Fusion036012028]
FEATURE [Part::MultiFuse] Fusion036012030  label="probe-slot"
  Shapes = -> [Cylinder025,Chamfer005011]
FEATURE [Part::MultiFuse] Fusion036012031  label="back-belt-mount"
  Shapes = -> [Chamfer003,Chamfer002]
FEATURE [Part::MultiFuse] Fusion036012034  label="back-wire-mounter"
  Shapes = -> [Cut036009013017007008008001,Cut036009013017007008008002]
FEATURE [Part::Box] Box063015  label="Cube073"
  AttacherType = Attacher::AttachEngine3D
  Height = 29
  Length = 15
  Placement = pos=(-7.5,-20,7) rot=(0,0,1;0rad)
  Width = 2
FEATURE [Part::Chamfer] Chamfer005021020  label="Chamfer005021021"
  Base = -> Box063015
  Edges = 3 edges r=1: [Edge1,Edge5,Edge9]
FEATURE [Part::Box] Box063016  label="Cube074"
  AttacherType = Attacher::AttachEngine3D
  Height = 5
  Length = 19
  Placement = pos=(-9.5,-26.5,34.5) rot=(0,0,1;0rad)
  Width = 8.5
FEATURE [Part::Box] Box063017  label="Cube075"
  AttacherType = Attacher::AttachEngine3D
  Height = 3.5
  Length = 19
  Placement = pos=(-9.5,-36.5,32) rot=(0,0,1;0rad)
  Width = 17.5
FEATURE [Part::Chamfer] Chamfer005021022  label="Chamfer005021023"
  Base = -> Box063017
  Edges = 3 edges r=2.5: [Edge4,Edge8,Edge9]
FEATURE [Part::Chamfer] Chamfer005021023  label="Chamfer005021024"
  Base = -> Box048
  Edges = 2 edges r=1: [Edge1,Edge5]
FEATURE [Part::MultiFuse] Fusion036012036
  Shapes = -> [Box063016,Cut013037]
FEATURE [Part::MultiFuse] Fusion036012037
  Shapes = -> [Chamfer005021020,Chamfer005021022,Chamfer005021023,Fusion036012036]
FEATURE [Part::Cut] Cut036009013017007008008015
  Base = -> Fusion036012037
  Tool = -> Fusion036012027
FEATURE [Part::Feature] Part__Feature041  label="5015-nozzle_fan"
  Placement = pos=(-9.975,-55.6,20.3) rot=(0,0,1;1.5708rad)
  shape: bbox 52.65 x 15 x 52.12 mm, 76 faces (baked)
FEATURE [Part::Cylinder] Cylinder060
  Angle = 360
  AttacherType = Attacher::AttachEngine3D
  Height = 10
  Placement = pos=(-14.7,-48.5,1.08e-14) rot=(1,0,0;1.5708rad)
  Radius = 2
FEATURE [Part::Cylinder] Cylinder061
  Angle = 360
  AttacherType = Attacher::AttachEngine3D
  Height = 10
  Placement = pos=(-5.4,-67,41.4) rot=(1,0,0;1.5708rad)
  Radius = 2
FEATURE [Part::Cylinder] Cylinder062
  Angle = 360
  AttacherType = Attacher::AttachEngine3D
  Height = 10
  Placement = pos=(37.6,-67,3.2) rot=(1,0,0;1.5708rad)
  Radius = 2
FEATURE [Part::Cylinder] Cylinder063
  Angle = 360
  AttacherType = Attacher::AttachEngine3D
  Height = 10
  Placement = pos=(24,-42.5,9.5) rot=(0,-1,0;1.5708rad)
  Radius = 1.3
FEATURE [Part::Cylinder] Cylinder064
  Angle = 360
  AttacherType = Attacher::AttachEngine3D
  Height = 17
  Placement = pos=(0,-43,35.75) rot=(1,0,0;1.5708rad)
  Radius = 1.65
FEATURE [Part::Box] Box063018  label="Cube076"
  AttacherType = Attacher::AttachEngine3D
  Height = 8
  Length = 9.1
  Placement = pos=(-19.23,-55.5,-3.5) rot=(0,0,1;0rad)
  Width = 5
FEATURE [Part::Box] Box063019  label="Cube077"
  AttacherType = Attacher::AttachEngine3D
  Height = 47.15
  Length = 52.48
  Placement = pos=(-10.13,-55.5,-1) rot=(0,0,1;0rad)
  Width = 5
FEATURE [Part::Chamfer] Chamfer005021024  label="Chamfer005021025"
  Base = -> Box063018
  Edges = 1 edges r=2: [Edge2]
FEATURE [Part::Chamfer] Chamfer005021025  label="Chamfer005021026"
  Base = -> Chamfer005021024
  Edges = 1 edges r=1.4: [Edge12]
FEATURE [Part::Cut] Cut036009013017007008008016
  Base = -> Chamfer005021025
  Tool = -> Cylinder060
FEATURE [Part::Feature] Part__Feature045  label="nozzle_fan_duct"
  Placement = pos=(0.025,-32.5,-13.5) rot=(0,0,1;0rad)
  shape: bbox 46.01 x 38.99 x 18.01 mm, 128 faces (baked)
FEATURE [Part::Box] Box063020  label="Cube078"
  AttacherType = Attacher::AttachEngine3D
  Height = 1.55
  Length = 9.5
  Placement = pos=(32.85,-55.5,-1.55) rot=(0,0,1;0rad)
  Width = 5
FEATURE [Part::Box] Box063021  label="Cube079"
  AttacherType = Attacher::AttachEngine3D
  Height = 7.5
  Length = 14
  Placement = pos=(-7,-50.5,32) rot=(0,0,1;0rad)
  Width = 5.5
FEATURE [Part::Box] Box063022  label="Cube080"
  AttacherType = Attacher::AttachEngine3D
  Height = 7
  Length = 2.9
  Placement = pos=(-9.5,-50.5,32.5) rot=(0,0,1;0rad)
  Width = 10.5
FEATURE [Part::Box] Box063023  label="Cube081"
  AttacherType = Attacher::AttachEngine3D
  Height = 7
  Length = 2.9
  Placement = pos=(6.6,-50.5,32.5) rot=(0,0,1;0rad)
  Width = 10.5
FEATURE [Part::Box] Box063024  label="Cube082"
  AttacherType = Attacher::AttachEngine3D
  Height = 4.5
  Length = 3.1
  Placement = pos=(-9.5,-50.5,7) rot=(0,0,1;0rad)
  Width = 10.5
FEATURE [Part::Box] Box063025  label="Cube083"
  AttacherType = Attacher::AttachEngine3D
  Height = 4.5
  Length = 13
  Placement = pos=(-6.5,-50.5,7) rot=(0,0,1;0rad)
  Width = 5.4
FEATURE [Part::Box] Box063027  label="Cube085"
  AttacherType = Attacher::AttachEngine3D
  Height = 5
  Length = 3
  Placement = pos=(17.5,-50.5,7) rot=(0,0,1;0rad)
  Width = 10.5
FEATURE [Part::Box] Box063028  label="Cube086"
  AttacherType = Attacher::AttachEngine3D
  Height = 4.5
  Length = 13
  Placement = pos=(6.5,-50.5,7) rot=(0,0,1;0rad)
  Width = 5.25
FEATURE [Part::Chamfer] Chamfer005021026  label="Chamfer005021027"
  Base = -> Box063021
  Edges = 2 edges r=0.5: [Edge4,Edge8]
FEATURE [Part::Cylinder] Cylinder065
  Angle = 360
  AttacherType = Attacher::AttachEngine3D
  Height = 1
  Placement = pos=(17.5,-42.5,9.5) rot=(0,-1,0;1.5708rad)
  Radius = 2.5
FEATURE [Part::Chamfer] Chamfer005021027  label="Chamfer005021028"
  Base = -> Cylinder065
  Edges = 1 edges r=0.6: [Edge1]
FEATURE [Part::Chamfer] Chamfer005021028  label="Chamfer005021029"
  Base = -> Box063027
  Edges = 2 edges r=1: [Edge11,Edge12]
FEATURE [Part::Chamfer] Chamfer005021029  label="Chamfer005021030"
  Base = -> Box063024
  Edges = 2 edges r=1: [Edge11,Edge12]
FEATURE [Part::Chamfer] Chamfer005021030  label="Chamfer005021031"
  Base = -> Box063022
  Edges = 2 edges r=1: [Edge11,Edge12]
FEATURE [Part::Chamfer] Chamfer005021031  label="Chamfer005021032"
  Base = -> Box063023
  Edges = 2 edges r=1: [Edge11,Edge12]
FEATURE [Part::MultiFuse] Fusion036012039002
  Shapes = -> [Chamfer005021027,Chamfer005021028]
FEATURE [Part::Cut] Cut036009013017007008008017
  Base = -> Fusion036012039002
  Tool = -> Cylinder063
FEATURE [Part::MultiFuse] Fusion036012039003
  Shapes = -> [Chamfer005021030,Chamfer005021026,Chamfer005021031]
FEATURE [Part::Cylinder] Cylinder066
  Angle = 360
  AttacherType = Attacher::AttachEngine3D
  Height = 3
  Placement = pos=(0,-42,35.75) rot=(1,0,0;1.5708rad)
  Radius = 2.1
FEATURE [Part::MultiFuse] Fusion036012039004
  Shapes = -> [Chamfer005021029,Box063025,Box063028,Cut036009013017007008008017]
FEATURE [Part::Chamfer] Chamfer005021032  label="Chamfer005021033"
  Base = -> Box063020
  Edges = 1 edges r=0.5: [Edge4]
FEATURE [Part::MultiFuse] Fusion036012039005
  Shapes = -> [Box063019,Cut036009013017007008008016,Chamfer005021032]
FEATURE [Part::MultiFuse] Fusion036012039006
  Shapes = -> [Fusion036012039003,Fusion036012039004,Fusion036012039005]
FEATURE [Part::MultiFuse] Fusion036012039007
  Placement = pos=(0,16.5,0) rot=(0,0,1;0rad)
  Shapes = -> [Cylinder062,Cylinder061]
FEATURE [Part::Cylinder] Cylinder067
  Angle = 360
  AttacherType = Attacher::AttachEngine3D
  Height = 17
  Placement = pos=(0,-52,35.75) rot=(1,0,0;1.5708rad)
  Radius = 3
FEATURE [Part::Cut] Cut036009013017007008008019
  Base = -> Fusion036012039006
  Tool = -> Fusion036012039007
FEATURE [Part::Cut] Cut036009013017007008008020
  Base = -> Cut036009013017007008008019
  Tool = -> Cylinder064
FEATURE [Part::Cut] Cut036009013017007008008021  label="grid-plate-base"
  Base = -> Cut036009013017007008008020
  Tool = -> Cylinder067
FEATURE [Part::Feature] Cut036009013017007008008021001  label="Cut036009013017007008008022"
  shape: bbox 61.58 x 15.5 x 49.65 mm, 61 faces (baked)
FEATURE [Part::Chamfer] Chamfer005021033  label="Chamfer005021034"
  Base = -> Cut036009013017007008008021001
  Edges = 2 edges r=2: [Edge2,Edge36]
FEATURE [Part::Box] Box063029  label="Cube087"
  AttacherType = Attacher::AttachEngine3D
  Height = 10
  Length = 50
  Placement = pos=(-0.65,-57,39.5) rot=(0,0,1;0rad)
  Width = 10
FEATURE [Part::Box] Box063030  label="Cube088"
  AttacherType = Attacher::AttachEngine3D
  Height = 31
  Length = 50
  Placement = pos=(9.5,-57,12) rot=(0,0,1;0rad)
  Width = 10
FEATURE [Part::Box] Box063031  label="Cube089"
  AttacherType = Attacher::AttachEngine3D
  Height = 31
  Length = 50
  Placement = pos=(20.5,-57,7.95) rot=(0,0,1;0rad)
  Width = 10
FEATURE [Part::Chamfer] Chamfer005021034  label="Chamfer005021035"
  Base = -> Box063029
  Edges = 1 edges r=2: [Edge4]
FEATURE [Part::Cut] Cut036009013017007008008021002
  Base = -> Chamfer005021033
  Tool = -> Chamfer005021034
FEATURE [Part::Chamfer] Chamfer005021035  label="Chamfer005021036"
  Base = -> Box063030
  Edges = 1 edges r=2: [Edge4]
FEATURE [Part::Cut] Cut036009013017007008008021003
  Base = -> Cut036009013017007008008021002
  Tool = -> Chamfer005021035
FEATURE [Part::Chamfer] Chamfer005021036  label="Chamfer005021037"
  Base = -> Box063031
  Edges = 1 edges r=2: [Edge4]
FEATURE [Part::Cut] Cut036009013017007008008021004
  Base = -> Cut036009013017007008008021003
  Tool = -> Chamfer005021036
FEATURE [Part::Chamfer] Chamfer005021037  label="Chamfer005021038"
  Base = -> Cut036009013017007008008021004
  Edges = 2 edges r=2: [Edge81,Edge94]
FEATURE [Part::Feature] Body001
  Placement = pos=(-0.315,-47.5,22) rot=(0.57735,-0.57735,0.57735;2.0944rad)
  shape: bbox 12.12 x 10 x 14 mm, 8 faces (baked)
FEATURE [Part::Feature] Fusion036012039008  label="2510-fan-2nd"
  Placement = pos=(20.52,-32.5,19.25) rot=(0.57735,0.57735,0.57735;2.0944rad)
  shape: bbox 10.5 x 25.76 x 25.8 mm, 132 faces, 2 solids (baked)
FEATURE [Part::Feature] Cut036009013017007008008021006  label="front-cable-mounter"
  Placement = pos=(0,1.1e-14,49.5) rot=(1,0,0;3.14159rad)
  shape: bbox 5 x 4 x 7 mm, 10 faces (baked)
FEATURE [Part::Box] Box063032  label="body-custom-support"
  AttacherType = Attacher::AttachEngine3D
  Height = 8
  Length = 0.2
  Placement = pos=(8.6,13.3,20.9) rot=(0,0,1;0rad)
  Width = 8
FEATURE [Part::Box] Box063033  label="Cube090"
  AttacherType = Attacher::AttachEngine3D
  Height = 32
  Length = 14
  Placement = pos=(-7,16.53,54) rot=(0,0,1;0rad)
  Width = 7
FEATURE [Part::Box] Box063034  label="Cube091"
  AttacherType = Attacher::AttachEngine3D
  Height = 4
  Length = 1
  Placement = pos=(-7,16.53,54) rot=(0,0,1;0rad)
  Width = 7
FEATURE [Part::Box] Box063035  label="Cube092"
  AttacherType = Attacher::AttachEngine3D
  Height = 4
  Length = 1
  Placement = pos=(6,16.53,54) rot=(0,0,1;0rad)
  Width = 7
FEATURE [Part::MultiFuse] Fusion036012039011002
  Placement = pos=(0,0,23) rot=(0,0,1;0rad)
  Shapes = -> [Box063035,Box063034]
FEATURE [Part::Feature] Fusion036012039011002001  label="Fusion036012039011003"
  Placement = pos=(0,0,11) rot=(0,0,1;0rad)
  shape: bbox 14 x 7 x 4 mm, 12 faces, 2 solids (baked)
FEATURE [Part::MultiFuse] Fusion036012039011002002
  Shapes = -> [Fusion036012039011002001,Fusion036012039011002]
FEATURE [Part::Chamfer] Chamfer005021038  label="Chamfer005021039"
  Base = -> Box063033
  Edges = 1 edges r=3: [Edge10]
FEATURE [Part::Cut] Cut036009013017007008008021005002
  Base = -> Chamfer005021038
  Tool = -> Fusion036012039011002002
FEATURE [Part::Cylinder] Cylinder068
  Angle = 360
  AttacherType = Attacher::AttachEngine3D
  Height = 29
  Placement = pos=(0,7.5,56.5) rot=(0,0,1;0rad)
  Radius = 11
FEATURE [Part::Chamfer] Chamfer005021040  label="Chamfer005021041"
  Base = -> Cylinder068
  Edges = 1 edges r=1: [Edge3]
FEATURE [Part::Chamfer] Chamfer005021041  label="Chamfer005021042"
  Base = -> Cut036009013017007008008021005002
  Edges = 13 edges r=0.99: [Edge7,Edge11,Edge17,Edge21,Edge28,Edge30,Edge32,Edge34,Edge35,Edge36,Edge38,Edge40,Edge42]
FEATURE [Part::Cut] Cut036009013017007008008021005003
  Base = -> Chamfer005021041
  Tool = -> Chamfer005021040
FEATURE [Part::Box] Box063037  label="Cube094"
  AttacherType = Attacher::AttachEngine3D
  Height = 10
  Length = 11
  Placement = pos=(-28,-6.5,44) rot=(0,0,1;0rad)
  Width = 13
FEATURE [Part::Cut] Cut036009013017007008008021005  label="fan-mount-r1"
  Base = -> Chamfer005021037
  Tool = -> Body001
FEATURE [Part::Feature] Cut036009013017007008008006001  label="extra-wire-mounter001"
  Placement = pos=(2.5,0,0) rot=(0,0,1;0rad)
  shape: bbox 10 x 5 x 2 mm, 11 faces (baked)
FEATURE [Part::MultiFuse] Fusion036012039011002004  label="hotend-wire-mounter-back"
  Placement = pos=(21,0,-5.5) rot=(0,0,1;0rad)
  Shapes = -> [Cut036009013017007008008006,Cut036009013017007008008006001]
FEATURE [Part::Chamfer] Chamfer005021045  label="hotend-cut"
  Base = -> Box063014
  Edges = 3 edges r=5: [Edge3,Edge7,Edge12]
FEATURE [Part::MultiFuse] Fusion036  label="rail-bolt"
  Shapes = -> [Cylinder033,Cylinder032,Cylinder031,Cylinder030]
FEATURE [Part::Box] Box063038  label="Cube095"
  AttacherType = Attacher::AttachEngine3D
  Height = 10.2
  Length = 10
  Placement = pos=(-24.3,-12.5,5) rot=(0,0,1;0rad)
  Width = 25
FEATURE [Part::Chamfer] Chamfer005021046  label="rail-block-screw-slot"
  Base = -> Box063038
  Edges = 2 edges r=1.5: [Edge1,Edge3]
FEATURE [Part::Feature] Cut036009013017007008008021005005006  label="dual-fan-adapter"
  Placement = pos=(17.25,-32.5,19.5) rot=(0,0,1;0rad)
  shape: bbox 3.5 x 25 x 25 mm, 25 faces (baked)
FEATURE [Part::Feature] Part__Feature112001002  label="2020-extrusion-pred"
  Placement = pos=(51.5,-10,18) rot=(0,-1,0;1.5708rad)
  shape: bbox 100 x 20 x 20 mm, 91 faces (baked)
FEATURE [Part::Feature] Fusion036012039011002007  label="MGN12H"
  Placement = pos=(-4.5,-4,18) rot=(0,0,1;0rad)
  shape: bbox 400 x 27 x 13 mm, 263 faces (baked)
FEATURE [Part::Box] Box063039  label="Cube096"
  AttacherType = Attacher::AttachEngine3D
  Height = 20
  Length = 152
  Placement = pos=(-200.5,-10,0) rot=(0,0,1;0rad)
  Width = 25
FEATURE [Part::Box] Box063040  label="Cube097"
  AttacherType = Attacher::AttachEngine3D
  Height = 20
  Length = 154
  Placement = pos=(51.5,-10,0) rot=(0,0,1;0rad)
  Width = 25
FEATURE [Part::MultiFuse] Fusion036012039011002008
  Shapes = -> [Box063040,Box063039]
FEATURE [Part::Cut] Cut036009013017007008008021005005007  label="MGN12H-pref"
  Base = -> Fusion036012039011002007
  Tool = -> Fusion036012039011002008
FEATURE [Part::Box] Box063041  label="Cube098"
  AttacherType = Attacher::AttachEngine3D
  Height = 17.35
  Length = 10
  Placement = pos=(23,1.45,7) rot=(0,0,1;0rad)
  Width = 10
FEATURE [Part::Box] Box063042  label="Cube099"
  AttacherType = Attacher::AttachEngine3D
  Height = 15.35
  Length = 10
  Placement = pos=(23,-28,0) rot=(0,0,1;0rad)
  Width = 39
FEATURE [Part::Cut] Cut013014
  Base = -> Cut013013
  Tool = -> Box019
FEATURE [Part::Cut] Cut036009013017007008008021005005008
  Base = -> Cut013014
  Tool = -> Chamfer005021009
FEATURE [Part::Cut] Cut036009013017007008008021005005009
  Base = -> Cut036009013017007008008021005005008
  Tool = -> Chamfer005021046
FEATURE [Part::MultiFuse] Fusion036012039011002015
  Shapes = -> [Chamfer004,Cut036009013017007008008021005005009]
FEATURE [Part::MultiFuse] Fusion036012039011002016  label="bolt-slot-rf"
  Shapes = -> [Cylinder018,Cylinder017,Cylinder016,Cylinder015]
FEATURE [Part::MultiFuse] Fusion036012039011002017  label="bolt-slot"
  Shapes = -> [Cylinder014,Cylinder011,Cylinder012,Cylinder013]
FEATURE [Part::MultiFuse] Fusion036012039011002019  label="front-nut-slot"
  Shapes = -> [Box024,Box021,Box022,Box023]
FEATURE [Part::Box] Box063043  label="Cube100"
  AttacherType = Attacher::AttachEngine3D
  Height = 17.35
  Length = 16
  Placement = pos=(17.5,-13.6,7) rot=(0,0,1;0rad)
  Width = 11
FEATURE [Part::Box] Box063044  label="Cube101"
  AttacherType = Attacher::AttachEngine3D
  Height = 15.35
  Length = 10
  Placement = pos=(23,10,-4.86) rot=(0,0,1;0rad)
  Width = 15
FEATURE [Part::MultiFuse] Fusion036012039011002020  label="side-cutout"
  Shapes = -> [Box063044,Box063043,Box063042,Box063041]
FEATURE [Part::Cut] Cut036009013017007008008021005005010
  Base = -> Fusion036012039011002015
  Tool = -> Fusion036012039011002020
FEATURE [Part::MultiFuse] Fusion036012039011002021
  Shapes = -> [Cut036009013017007008008021005005010,Fusion036012039011002016]
FEATURE [Part::Cut] Cut036009013017007008008021005005011
  Base = -> Fusion036012039011002021
  Tool = -> Fusion036012039011002017
FEATURE [Part::Cut] Cut036009013017007008008021005005012
  Base = -> Cut036009013017007008008021005005011
  Tool = -> Fusion036012039011002019
FEATURE [Part::Chamfer] Chamfer005021047
  Base = -> Cut036009013017007008008021005005012
  Edges = 2 edges r=3: [Edge80,Edge192]
FEATURE [Part::Cut] Cut036009013017007008008021005005013
  Base = -> Chamfer005021047
  Tool = -> Chamfer005021045
FEATURE [Part::Cut] Cut036009013017007008008021005005014
  Base = -> Cut036009013017007008008021005005013
  Tool = -> Fusion036001
FEATURE [Part::Cut] Cut036009013017007008008021005005015
  Base = -> Cut036009013017007008008021005005014
  Tool = -> Cylinder049
FEATURE [Part::Cut] Cut036009013017007008008021005005020  label="extruder-mounter"
  Base = -> Cut036009013017007008008015
  Tool = -> Cylinder066
FEATURE [Part::MultiFuse] Fusion036012039011002022  label="cable-mounter-cmb"
  Shapes = -> [Cut036009013017007008008021006,Fusion036012034,Fusion036012039011002004]
FEATURE [Part::MultiFuse] Fusion036012039011002023
  Shapes = -> [Cut036009013017007008008021005005015,Fusion036012039011002022]
FEATURE [Part::MultiFuse] Fusion036012039011002024
  Shapes = -> [Fusion036012039011002023,Fusion036012031]
FEATURE [Part::Cut] Cut036009013017007008008021005005021
  Base = -> Fusion036012039011002024
  Tool = -> Fusion036012010
FEATURE [Part::Cut] Cut036009013017007008008021005005022
  Base = -> Cut036009013017007008008021005005021
  Tool = -> Fusion026
FEATURE [Part::Cut] Cut036009013017007008008021005005023
  Base = -> Cut036009013017007008008021005005022
  Tool = -> Fusion036012030
FEATURE [Part::Cut] Cut036009013017007008008021005005024
  Base = -> Cut036009013017007008008021005005023
  Tool = -> Fusion036012029
FEATURE [Part::MultiFuse] Fusion036012039011002025  label="body-base"
  Shapes = -> [Cut036009013017007008008021005005024,Cut036009013017007008008021005005020]
FEATURE [Part::Feature] Fusion036012039011002025001  label="body-r1-f5"
  shape: bbox 56 x 74.5 x 49.5 mm, 365 faces (baked)
FEATURE [Part::Box] Box063045  label="Cube102"
  AttacherType = Attacher::AttachEngine3D
  Height = 24
  Length = 10
  Placement = pos=(-30,-20,27) rot=(0,0,1;0rad)
  Width = 10
FEATURE [Part::Feature] Part__Feature112001003  label="X_BeltHolder_LH003"
  Placement = pos=(8.21,0.35,12.0001) rot=(0,0,1;0rad)
  shape: bbox 7.277 x 6.5 x 22.78 mm, 35 faces (baked)
FEATURE [Part::Cut] Cut036009013017007008008021005005025
  Base = -> Chamfer005021011
  Tool = -> Cylinder048
FEATURE [Part::Cylinder] Cylinder069
  Angle = 360
  AttacherType = Attacher::AttachEngine3D
  Height = 13
  Placement = pos=(-22.45,-9.5,48) rot=(0,0,1;0rad)
  Radius = 1.65
FEATURE [Part::MultiFuse] Fusion036012039011002025003
  Shapes = -> [Cut036009013017007008008005,Cut036009013017007008008004]
FEATURE [Part::Box] Box063046  label="Cube103"
  AttacherType = Attacher::AttachEngine3D
  Height = 8
  Length = 10.5
  Placement = pos=(-28,-13.5,40) rot=(0,0,1;0rad)
  Width = 7.5
FEATURE [Part::MultiFuse] Fusion036012039011002025006
  Shapes = -> [Part__Feature090001002,Part__Feature112001003]
FEATURE [Part::Chamfer] Chamfer005021049
  Base = -> Box063046
  Edges = 2 edges r=1: [Edge3,Edge7]
FEATURE [Part::Cut] Cut036009013017007008008021005005032
  Base = -> Chamfer005021049
  Tool = -> Cylinder047
FEATURE [Part::MultiFuse] Fusion036012039011002025007  label="belt-fl-mod"
  Shapes = -> [Fusion036012039011002025006,Cut036009013017007008008021005005032]
FEATURE [Part::Cylinder] Cylinder070
  Angle = 360
  AttacherType = Attacher::AttachEngine3D
  Height = 13
  Placement = pos=(-22.45,-9.5,55) rot=(0,0,1;0rad)
  Radius = 3
FEATURE [Part::Cut] Cut036009013017007008008021005005033
  Base = -> Cut036009013017007008008021005005025
  Tool = -> Box062
FEATURE [Part::Cut] Cut036009013017007008008021005005034
  Base = -> Cut036009013017007008008021005005033
  Tool = -> Box063037
FEATURE [Part::Cut] Cut036009013017007008008021005005035
  Base = -> Cut036009013017007008008021005005034
  Tool = -> Cylinder070
FEATURE [Part::Cut] Cut036009013017007008008021005005036
  Base = -> Cut036009013017007008008021005005035
  Tool = -> Cylinder069
FEATURE [Part::Cylinder] Cylinder071
  Angle = 360
  AttacherType = Attacher::AttachEngine3D
  Height = 6
  Placement = pos=(22.5,-13.5,51.5) rot=(0,0,1;0rad)
  Radius = 3
FEATURE [Part::Cylinder] Cylinder072
  Angle = 360
  AttacherType = Attacher::AttachEngine3D
  Height = 10
  Placement = pos=(-12,17.5,54.5) rot=(0,0,1;0rad)
  Radius = 3
FEATURE [Part::Cylinder] Cylinder073
  Angle = 360
  AttacherType = Attacher::AttachEngine3D
  Height = 6
  Placement = pos=(22.5,17.5,51.5) rot=(0,0,1;0rad)
  Radius = 3
FEATURE [Part::MultiFuse] Fusion036012039011002025008
  Shapes = -> [Cut036009013017007008008021005005036,Box053]
FEATURE [Part::Cut] Cut036009013017007008008021005005037
  Base = -> Fusion036012039011002025008
  Tool = -> Cylinder050
FEATURE [Part::MultiFuse] Fusion036012039011002025009
  Shapes = -> [Cut036009013017007008008021005005037,Fusion036012039011002025003]
FEATURE [Part::MultiFuse] Fusion036012039011002025010
  Shapes = -> [Cylinder053,Cylinder052,Cylinder051]
FEATURE [Part::MultiFuse] Fusion036012039011002025011
  Shapes = -> [Fusion036012039011002025009,Cut036009013017007008008021005003]
FEATURE [Part::Chamfer] Chamfer005021050
  Base = -> Fusion036012039011002025011
  Edges = 3 edges r=1.99: [Edge70,Edge71,Edge72]
FEATURE [Part::Cut] Cut036009013017007008008021005005038
  Base = -> Chamfer005021050
  Tool = -> Fusion036012039011002025010
FEATURE [Part::Cut] Cut036009013017007008008021005005039  label="cap-r1-f3"
  Base = -> Cut036009013017007008008021005005038
  Tool = -> Fusion036012011
FEATURE [Part::Box] Box063047  label="Cube104"
  AttacherType = Attacher::AttachEngine3D
  Height = 10
  Length = 17
  Placement = pos=(-30,-6.5,39) rot=(0,0,1;0rad)
  Width = 10
FEATURE [Part::Cut] Cut036009013017007008008021005005040
  Base = -> Fusion036012039011002025007
  Tool = -> Box063047
FEATURE [Part::Cylinder] Cylinder074
  Angle = 360
  AttacherType = Attacher::AttachEngine3D
  Height = 4
  Placement = pos=(-17,-19,17.5) rot=(1,0,0;1.5708rad)
  Radius = 4
FEATURE [Part::Box] Box063048  label="Cube105"
  AttacherType = Attacher::AttachEngine3D
  Height = 6
  Length = 8
  Placement = pos=(-21,-23,17.5) rot=(0,0,1;0rad)
  Width = 4
FEATURE [Part::Box] Box063050  label="Cube107"
  AttacherType = Attacher::AttachEngine3D
  Height = 15
  Length = 2.5
  Placement = pos=(-94,-22,8.5) rot=(0,0,1;0rad)
  Width = 6
FEATURE [Part::Box] Box063051  label="Cube108"
  AttacherType = Attacher::AttachEngine3D
  Height = 15
  Length = 16
  Placement = pos=(-94,-22,8.5) rot=(0,0,1;0rad)
  Width = 3
FEATURE [Part::Box] Box063052  label="Cube109"
  AttacherType = Attacher::AttachEngine3D
  Height = 15
  Length = 15
  Placement = pos=(-115,-22,24) rot=(0,0,1;0rad)
  Width = 6
FEATURE [Part::Box] Box063053  label="Cube110"
  AttacherType = Attacher::AttachEngine3D
  Height = 15
  Length = 11
  Placement = pos=(-84.5,-22,13.5) rot=(0,0,1;0rad)
  Width = 6
FEATURE [Part::Chamfer] Chamfer005021054
  Base = -> Box063051
  Edges = 1 edges r=5: [Edge8]
FEATURE [Part::Chamfer] Chamfer005021055
  Base = -> Box063052
  Edges = 1 edges r=10: [Edge8]
  Placement = pos=(15.5,0,-10.5) rot=(0,0,1;0rad)
FEATURE [Part::Box] Box063054  label="Cube111"
  AttacherType = Attacher::AttachEngine3D
  Height = 10
  Length = 10
  Placement = pos=(-96,-19,18.5) rot=(0,0,1;0rad)
  Width = 10
FEATURE [Part::Chamfer] Chamfer005021057
  Base = -> Box063054
  Edges = 1 edges r=3: [Edge9]
  Placement = pos=(0,0,-5.5) rot=(0,0,1;0rad)
FEATURE [Part::MultiFuse] Fusion036012039011002025017
  Shapes = -> [Chamfer005021054,Box063050]
FEATURE [Part::Cut] Cut036009013017007008008021005005044002
  Base = -> Fusion036012039011002025017
  Tool = -> Chamfer005021055
FEATURE [Part::Cut] Cut036009013017007008008021005005044003
  Base = -> Cut036009013017007008008021005005044002
  Tool = -> Box063053
FEATURE [Part::Cut] Cut036009013017007008008021005005044004
  Base = -> Cut036009013017007008008021005005044003
  Placement = pos=(63,0,0) rot=(0,0,1;0rad)
  Tool = -> Chamfer005021057
FEATURE [Part::Cylinder] Cylinder076
  Angle = 360
  AttacherType = Attacher::AttachEngine3D
  Height = 4
  Placement = pos=(-17,-19,23.5) rot=(1,0,0;1.5708rad)
  Radius = 4
FEATURE [Part::Box] Box063055  label="Cube112"
  AttacherType = Attacher::AttachEngine3D
  Height = 2.5
  Length = 3.3
  Placement = pos=(-18.65,-23,17.5) rot=(0,0,1;0rad)
  Width = 4
FEATURE [Part::Cylinder] Cylinder077
  Angle = 360
  AttacherType = Attacher::AttachEngine3D
  Height = 4
  Placement = pos=(-17,-19,19.5) rot=(1,0,0;1.5708rad)
  Radius = 1.65
FEATURE [Part::Cylinder] Cylinder078
  Angle = 360
  AttacherType = Attacher::AttachEngine3D
  Height = 4
  Placement = pos=(-17,-19,17.5) rot=(1,0,0;1.5708rad)
  Radius = 1.65
FEATURE [Part::MultiFuse] Fusion036012039011002025018
  Shapes = -> [Box063048,Cylinder076,Cylinder074]
FEATURE [Part::Feature] Fusion036012039011002025018001  label="Fusion036012039011002025019"
  shape: bbox 8 x 4 x 14 mm, 6 faces (baked)
FEATURE [Part::Chamfer] Chamfer005021058
  Base = -> Fusion036012039011002025018001
  Edges = 4 edges r=1: [Edge1,Edge5,Edge8,Edge11]
FEATURE [Part::Cut] Cut036009013017007008008021005005044005
  Base = -> Chamfer005021058
  Tool = -> Cylinder077
FEATURE [Part::MultiFuse] Fusion036012039011002025018002  label="fixed-probe-20"
  Shapes = -> [Cut036009013017007008008021005005044004,Cut036009013017007008008021005005044005,Fusion034]
FEATURE [Part::Feature] Cut036009013017007008008021005005044006  label="fan-mount-r002"
  shape: bbox 61.58 x 15.5 x 49.65 mm, 84 faces (baked)
